# Revit family: Graypants_Scraplights_Classics_Skew_13_15_22_Sconce_R21_0925
name_source: partatom
category: Lighting Fixtures
units: mm (PartAtom-declared; Revit-internal decimal feet)

## family parameters
Cut with Voids When Loaded = No
Host = Face
Light Source = Yes
Part Type = Normal
Room Calculation Point = No
Round Connector Dimension = Use Diameter
Shared = No

## types (3) — shared parameters
Color Filter = 16777215
Default Elevation = 4' - 0"
Dimming Lamp Color Temperature Shift = <None>
Emit Shape Visible in Rendering = No
Graypants_Cord/Canopy_Finish_Options = White | Black
Graypants_Manufacturer = Graypants
Graypants_Shade_Finish_Options = Natural Cardboard | Blonde Cardboard | White Cardboard
Graypants_URL = www.graypants.com

## per-type parameters (varying)
| type | Emit from Rectangle Length | Emit from Rectangle Width | Graypants_Model | Graypants_Skew13_Visible | Graypants_Skew15_Visible | Graypants_Skew22_Visible | Light Source Symbol Size |
| Graypants_Scraplights_Skew13_Sconce | 1' - 4 7/8" | 2' - 0" | Scraplights_Classics_Skew_13 | Yes | No | No | 1' - 1" |
| Graypants_Scraplights_Skew15_Sconce | 0' - 9 25/32" | 0' - 4" | Scraplights_Classics_Skew_15 | No | Yes | No | 1' - 3" |
| Graypants_Scraplights_Skew22_Sconce | 1' - 2 1/4" | 2' - 0" | Scraplights_Classics_Skew_22 | No | No | Yes | 1' - 10" |

## geometry (parser evidence)
native form markers: Sweep x10
no freeform markers — native parametric forms only
